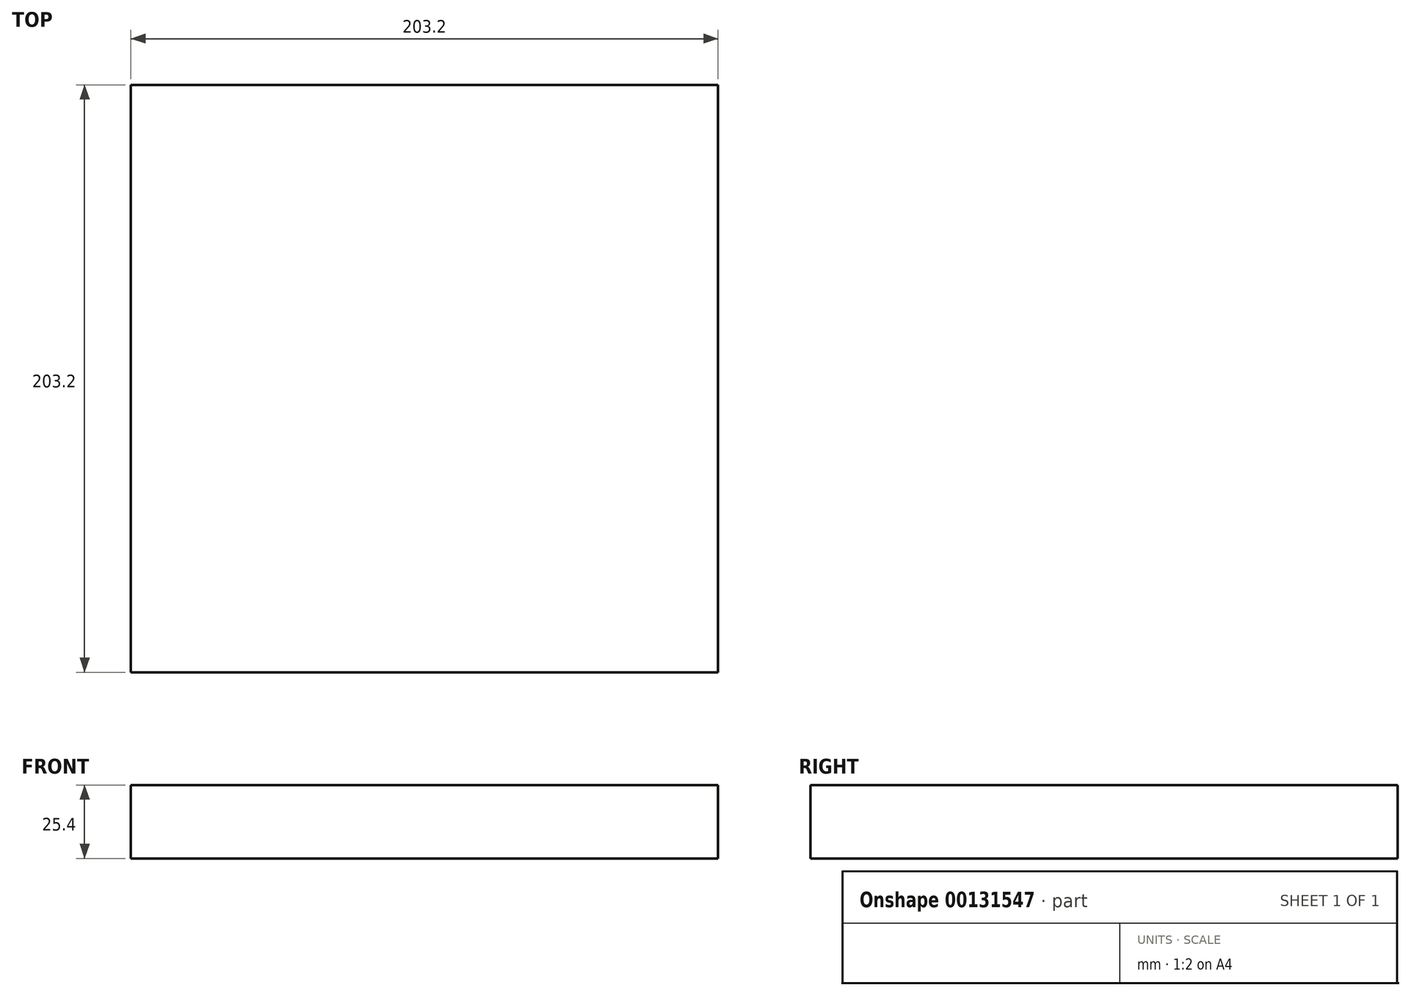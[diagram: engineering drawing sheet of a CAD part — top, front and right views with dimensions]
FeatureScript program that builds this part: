
annotation { "Feature Type Name" : "Feature", "Feature Type Description" : "" }
export const myFeature = defineFeature(function(context is Context, id is Id, definition is map)
    precondition{}
    {
        {
            var Q0;
            Q0=qCreatedBy(makeId("Top.planeOp"),FACE);
            var sketch = newSketch(context, id + "F0", { "sketchPlane" : qUnion([Q0])});
            skLineSegment(sketch, "E0.bottom", {"start": v(101.6, 101.6) * mm, "end": v(-101.6, 101.6) * mm});
            skLineSegment(sketch, "E0.top", {"start": v(101.6, -101.6) * mm, "end": v(-101.6, -101.6) * mm});
            skLineSegment(sketch, "E0.left", {"start": v(101.6, 101.6) * mm, "end": v(101.6, -101.6) * mm});
            skLineSegment(sketch, "E0.right", {"start": v(-101.6, 101.6) * mm, "end": v(-101.6, -101.6) * mm});
            skPoint(sketch, "E0.middle", {"position": v(0, 0) * mm});
            skSolve(sketch);
        }
        {
            var Q0;
            Q0=makeQuery(id+"F0.imprint","IMPRINT",FACE,{"disambiguationData":[TD([[makeQuery(id+"F0.imprint","IMPRINT",EDGE,{"derivedFrom":sQuery(id+"F0.wireOp",EDGE,"E0.bottom")}),1.0]])]});
            extrude(context, id + "F1", {"entities" : qUnion([Q0]), "depth" : 25.4 * mm});
        }
    });
